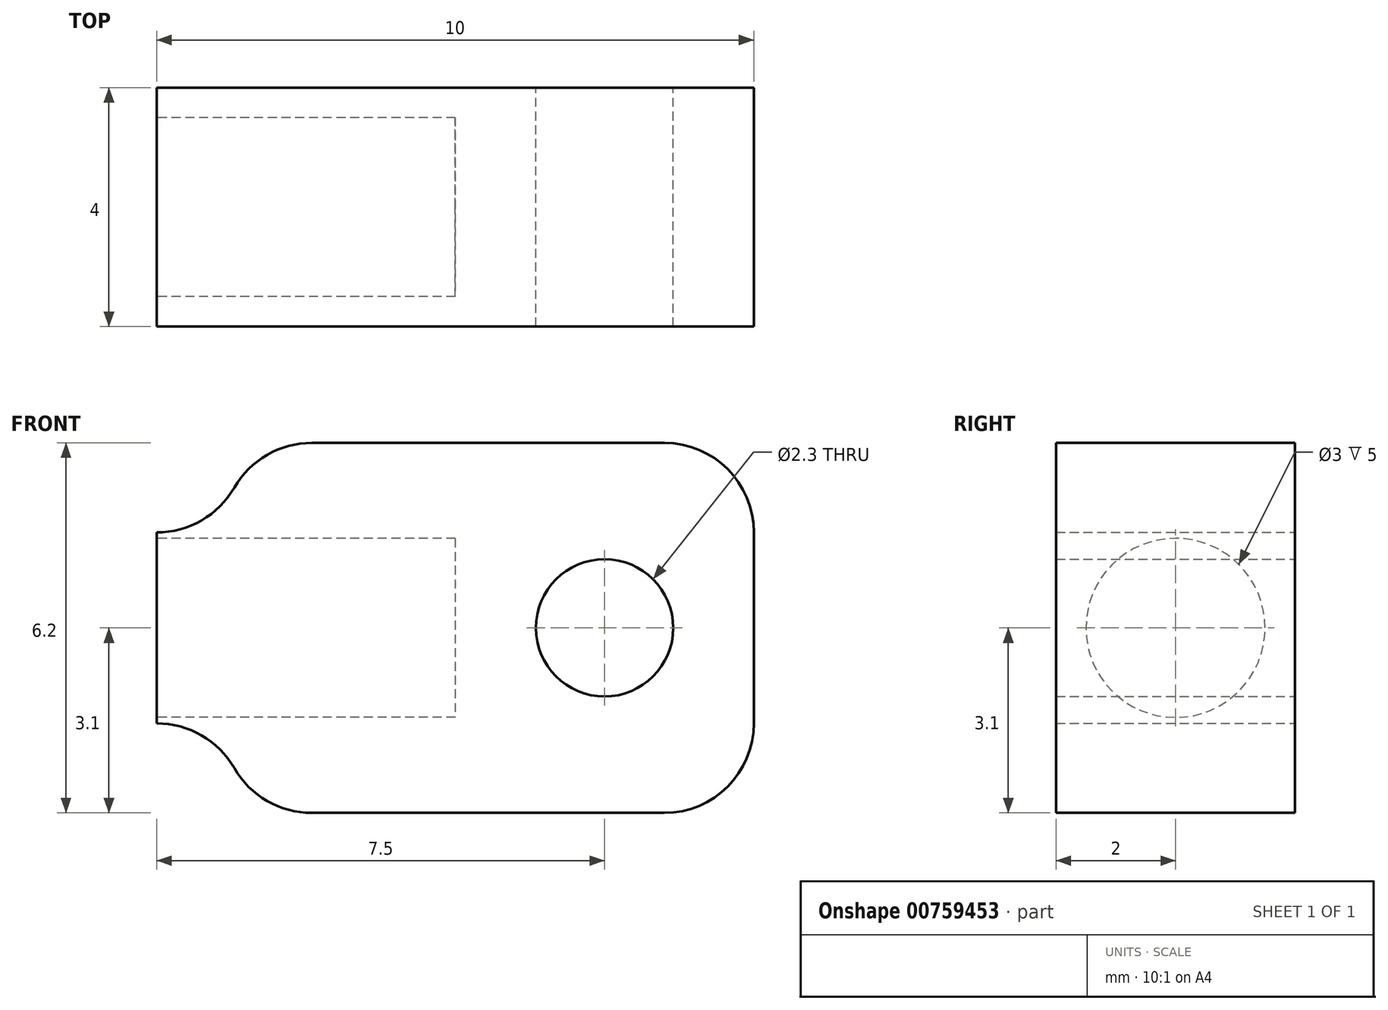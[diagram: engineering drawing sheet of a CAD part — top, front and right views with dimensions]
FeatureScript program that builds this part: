
annotation { "Feature Type Name" : "Feature", "Feature Type Description" : "" }
export const myFeature = defineFeature(function(context is Context, id is Id, definition is map)
    precondition{}
    {
        {
            var Q0;
            Q0=qCreatedBy(makeId("Front.planeOp"),FACE);
            var sketch = newSketch(context, id + "F0", { "sketchPlane" : qUnion([Q0])});
            skLineSegment(sketch, "E0.bottom", {"start": v(5, 3.1) * mm, "end": v(-3.5, 3.1) * mm});
            skLineSegment(sketch, "E0.top", {"start": v(5, -3.1) * mm, "end": v(-3.5, -3.1) * mm});
            skLineSegment(sketch, "E0.left", {"start": v(5, 3.1) * mm, "end": v(5, -3.1) * mm});
            skLineSegment(sketch, "E0.right", {"start": v(-5, 1.6) * mm, "end": v(-5, -1.6) * mm});
            skPoint(sketch, "E0.middle", {"position": v(0, 0) * mm});
            skCircle(sketch, "E1", {"center": v(2.5, 0) * mm, "radius": 1.15 * mm});
            skPoint(sketch, "E2.middle", {"position": v(-2.5, 0) * mm});
            skPoint(sketch, "E2.bottom.end.orphan", {"position": v(-5, 1.6) * mm});
            skPoint(sketch, "E3.orphan", {"position": v(0, 1.6) * mm});
            skPoint(sketch, "E2.top.end.orphan", {"position": v(-5, -1.6) * mm});
            skPoint(sketch, "E2.top.start.orphan", {"position": v(0, -1.6) * mm});
            skLineSegment(sketch, "E4", {"start": v(-5.81, -1.6) * mm, "end": v(-3.9, -1.6) * mm, "construction": true});
            skLineSegment(sketch, "E5", {"start": v(-3.5, -2.23) * mm, "end": v(-3.5, -3.95) * mm, "construction": true});
            skArc(sketch, "E6", {"start": v(-3.5, -3.1) * mm, "mid": v(-3.94, -2.04) * mm, "end": v(-5, -1.6) * mm});
            skArc(sketch, "E7.MirrorCS", {"start": v(-3.5, 3.1) * mm, "mid": v(-3.94, 2.04) * mm, "end": v(-5, 1.6) * mm});
            skSolve(sketch);
        }
        {
            var Q0;
            Q0 = qSketchRegion(id + "F0", true);
            extrude(context, id + "F1", {"entities" : qUnion([Q0]), "depth" : 4 * mm, "offsetDistance" : 25 * mm});
        }
        {
            var Q0;
            Q0=makeQuery(id+"F1.opExtrude","SWEPT_FACE",FACE,{"disambiguationData":[OSD([sQuery(id+"F0.wireOp",EDGE,"E0.right")])]});
            var sketch = newSketch(context, id + "F2", { "sketchPlane" : qUnion([Q0])});
            skCircle(sketch, "E8", {"center": v(2, 0) * mm, "radius": 1.5 * mm});
            skSolve(sketch);
        }
        {
            var Q0;
            Q0 = qSketchRegion(id + "F2", true);
            extrude(context, id + "F3", {"entities" : qUnion([Q0]), "operationType" : NewBodyOperationType.REMOVE, "oppositeDirection" : true, "depth" : 5 * mm, "offsetDistance" : 25 * mm});
        }
        {
            var Q0;
            Q0=makeQuery(id+"F1.opExtrude","SWEPT_EDGE",EDGE,{"disambiguationData":[OSD([sQuery(id+"F0.wireOp",EDGE,"E0.bottom"),sQuery(id+"F0.wireOp",EDGE,"E7.MirrorCS")])]});
            var Q1;
            Q1=makeQuery(id+"F1.opExtrude","SWEPT_EDGE",EDGE,{"disambiguationData":[OSD([sQuery(id+"F0.wireOp",EDGE,"E0.top"),sQuery(id+"F0.wireOp",EDGE,"E6")])]});
            var Q2;
            Q2=makeQuery(id+"F1.opExtrude","SWEPT_EDGE",EDGE,{"disambiguationData":[OSD([sQuery(id+"F0.wireOp",EDGE,"E0.bottom"),sQuery(id+"F0.wireOp",EDGE,"E0.left")])]});
            var Q3;
            Q3=makeQuery(id+"F1.opExtrude","SWEPT_EDGE",EDGE,{"disambiguationData":[OSD([sQuery(id+"F0.wireOp",EDGE,"E0.top"),sQuery(id+"F0.wireOp",EDGE,"E0.left")])]});
            fillet(context, id + "F4", {"entities" : qUnion([Q0, Q1, Q2, Q3]), "radius" : 1.5 * mm, "tangentPropagation" : true, "allowEdgeOverflow" : false});
        }
    });
